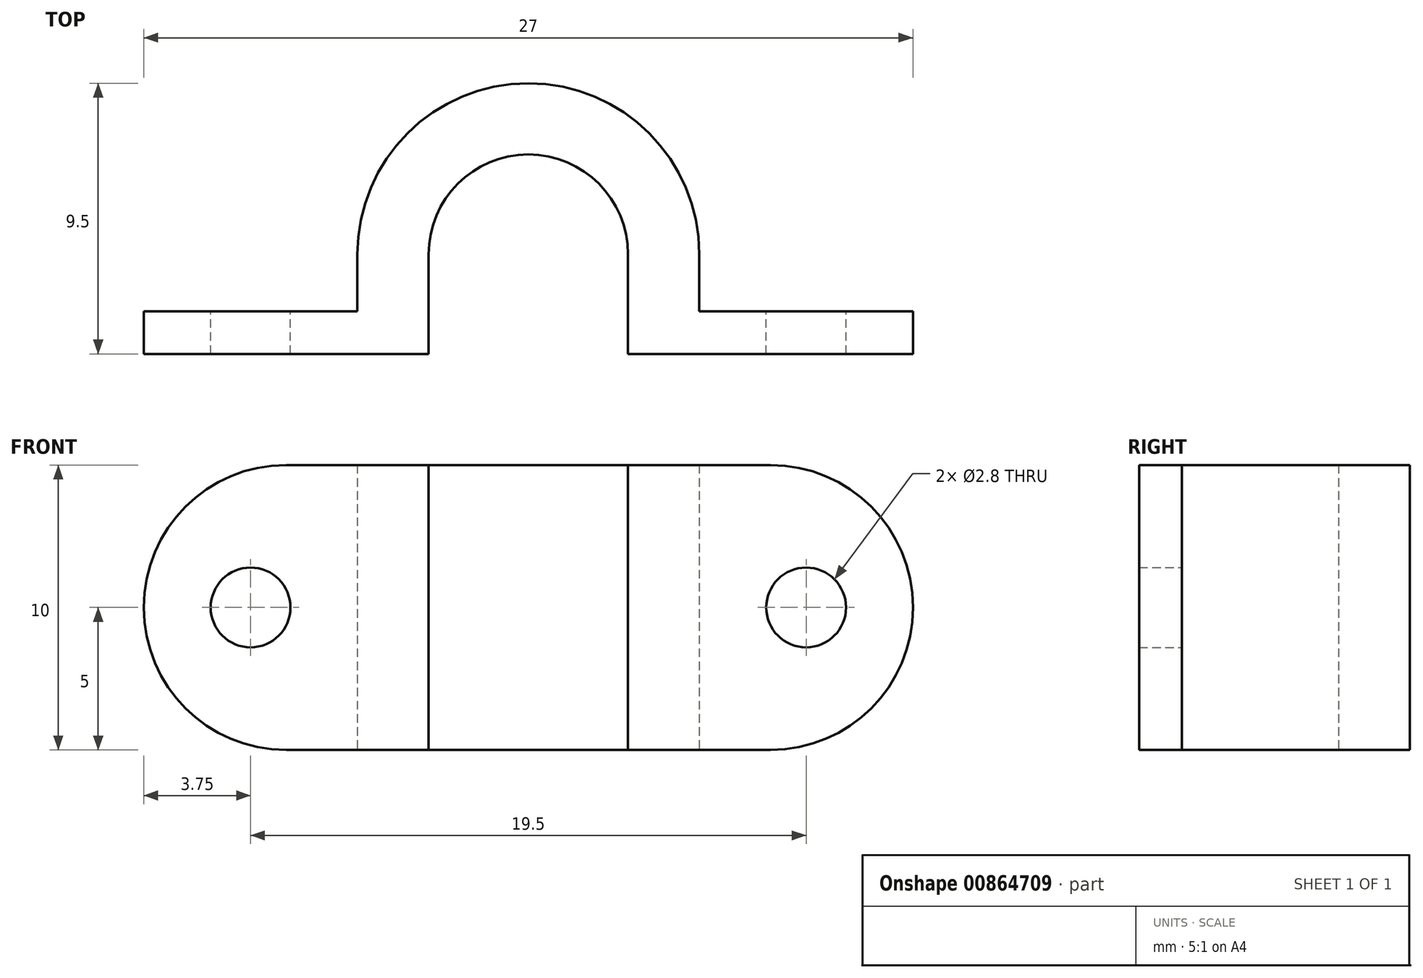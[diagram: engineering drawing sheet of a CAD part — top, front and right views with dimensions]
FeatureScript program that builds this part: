
annotation { "Feature Type Name" : "Feature", "Feature Type Description" : "" }
export const myFeature = defineFeature(function(context is Context, id is Id, definition is map)
    precondition{}
    {
        {
            var Q0;
            Q0=qCreatedBy(makeId("Top.planeOp"),FACE);
            var sketch = newSketch(context, id + "F0", { "sketchPlane" : qUnion([Q0])});
            skArc(sketch, "E0", {"start": v(3.5, 0) * mm, "mid": v(0, 3.5) * mm, "end": v(-3.5, 0) * mm});
            skLineSegment(sketch, "E1", {"start": v(-3.5, 0) * mm, "end": v(-3.5, -3.5) * mm});
            skLineSegment(sketch, "E2", {"start": v(-3.5, -3.5) * mm, "end": v(3.5, -3.5) * mm});
            skLineSegment(sketch, "E3", {"start": v(3.5, -3.5) * mm, "end": v(3.5, 0) * mm});
            skLineSegment(sketch, "E4", {"start": v(-3.5, -3.5) * mm, "end": v(-13.5, -3.5) * mm});
            skLineSegment(sketch, "E5", {"start": v(-13.5, -3.5) * mm, "end": v(-13.5, -2) * mm});
            skLineSegment(sketch, "E6", {"start": v(-13.5, -2) * mm, "end": v(-6, -2) * mm});
            skLineSegment(sketch, "E7", {"start": v(-6, -2) * mm, "end": v(-6, 0) * mm});
            skArc(sketch, "E8", {"start": v(6, 0) * mm, "mid": v(0, 6) * mm, "end": v(-6, 0) * mm});
            skLineSegment(sketch, "E9", {"start": v(3.5, -3.5) * mm, "end": v(13.5, -3.5) * mm});
            skLineSegment(sketch, "E10", {"start": v(13.5, -3.5) * mm, "end": v(13.5, -2) * mm});
            skLineSegment(sketch, "E11", {"start": v(13.5, -2) * mm, "end": v(6, -2) * mm});
            skLineSegment(sketch, "E12", {"start": v(6, -2) * mm, "end": v(6, 0) * mm});
            skSolve(sketch);
        }
        {
            var Q0;
            Q0=makeQuery(id+"F0.imprint","IMPRINT",FACE,{"disambiguationData":[TD([[makeQuery(id+"F0.imprint","IMPRINT",EDGE,{"derivedFrom":sQuery(id+"F0.wireOp",EDGE,"E0")}),-1.0]])]});
            extrude(context, id + "F1", {"entities" : qUnion([Q0]), "depth" : 10 * mm, "offsetDistance" : 25 * mm});
        }
        {
            var Q0;
            Q0=makeQuery(id+"F1.opExtrude","SWEPT_FACE",FACE,{"disambiguationData":[OSD([sQuery(id+"F0.wireOp",EDGE,"E6")])]});
            var sketch = newSketch(context, id + "F2", { "sketchPlane" : qUnion([Q0])});
            skLineSegment(sketch, "E13.0.0", {"start": v(6, 0) * mm, "end": v(13.5, 0) * mm});
            skLineSegment(sketch, "E13.0.1", {"start": v(13.5, 0) * mm, "end": v(13.5, 10) * mm});
            skLineSegment(sketch, "E13.0.2", {"start": v(13.5, 10) * mm, "end": v(6, 10) * mm});
            skLineSegment(sketch, "E13.0.3", {"start": v(6, 10) * mm, "end": v(6, 0) * mm});
            skCircle(sketch, "E14", {"center": v(9.75, 5) * mm, "radius": 1.4 * mm});
            skPoint(sketch, "E14.centerSnap0", {"position": v(13.5, 5) * mm});
            skPoint(sketch, "E14.centerSnap1", {"position": v(9.75, 0) * mm});
            skLineSegment(sketch, "E15.0.0", {"start": v(-13.5, 0) * mm, "end": v(-6, 0) * mm});
            skLineSegment(sketch, "E15.0.1", {"start": v(-6, 0) * mm, "end": v(-6, 10) * mm});
            skLineSegment(sketch, "E15.0.2", {"start": v(-6, 10) * mm, "end": v(-13.5, 10) * mm});
            skLineSegment(sketch, "E15.0.3", {"start": v(-13.5, 10) * mm, "end": v(-13.5, 0) * mm});
            skCircle(sketch, "E16", {"center": v(-9.75, 5) * mm, "radius": 1.4 * mm});
            skPoint(sketch, "E16.centerSnap0", {"position": v(-13.5, 5) * mm});
            skPoint(sketch, "E16.centerSnap1", {"position": v(-9.75, 0) * mm});
            skSolve(sketch);
        }
        {
            var Q0;
            Q0=makeQuery(id+"F2.imprint","IMPRINT",FACE,{"disambiguationData":[TD([[makeQuery(id+"F2.imprint","IMPRINT",EDGE,{"derivedFrom":sQuery(id+"F2.wireOp",EDGE,"E14")}),1.0]])]});
            var Q1;
            Q1=makeQuery(id+"F2.imprint","IMPRINT",FACE,{"disambiguationData":[TD([[makeQuery(id+"F2.imprint","IMPRINT",EDGE,{"derivedFrom":sQuery(id+"F2.wireOp",EDGE,"E16")}),1.0]])]});
            extrude(context, id + "F3", {"entities" : qUnion([Q0, Q1]), "operationType" : NewBodyOperationType.REMOVE, "oppositeDirection" : true, "depth" : 25 * mm, "offsetDistance" : 25 * mm});
        }
        {
            var Q0;
            Q0=makeQuery(id+"F1.opExtrude","CAP_EDGE",EDGE,{"disambiguationData":[OSD([sQuery(id+"F0.wireOp",EDGE,"E5")])],"isStart":false});
            var Q1;
            Q1=makeQuery(id+"F1.opExtrude","CAP_EDGE",EDGE,{"disambiguationData":[OSD([sQuery(id+"F0.wireOp",EDGE,"E10")])],"isStart":false});
            var Q2;
            Q2=makeQuery(id+"F1.opExtrude","CAP_EDGE",EDGE,{"disambiguationData":[OSD([sQuery(id+"F0.wireOp",EDGE,"E5")])],"isStart":true});
            var Q3;
            Q3=makeQuery(id+"F1.opExtrude","CAP_EDGE",EDGE,{"disambiguationData":[OSD([sQuery(id+"F0.wireOp",EDGE,"E10")])],"isStart":true});
            fillet(context, id + "F4", {"entities" : qUnion([Q0, Q1, Q2, Q3]), "radius" : 5 * mm, "tangentPropagation" : true, "allowEdgeOverflow" : false});
        }
    });
